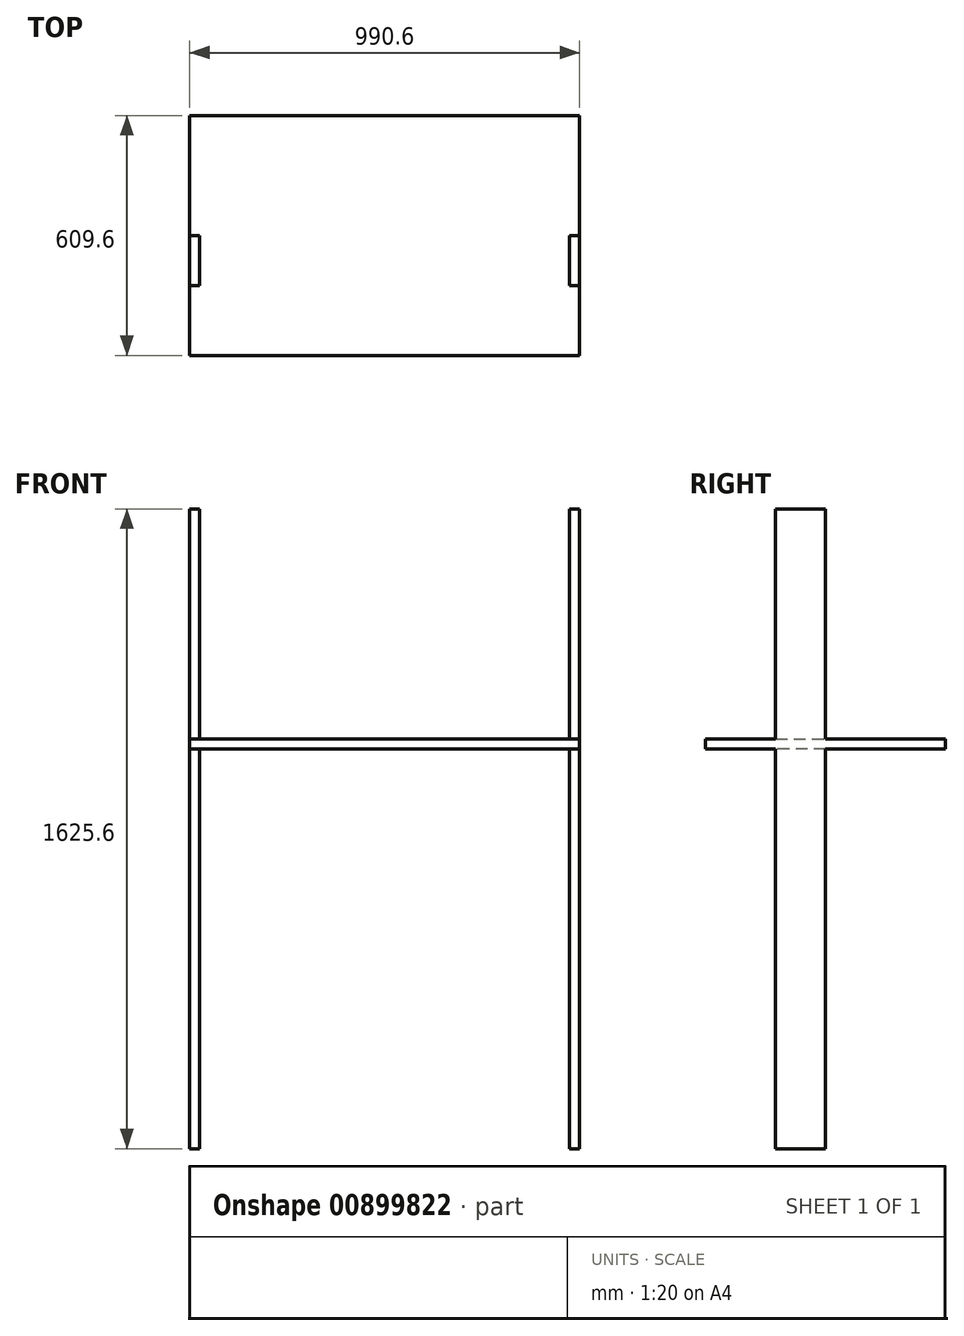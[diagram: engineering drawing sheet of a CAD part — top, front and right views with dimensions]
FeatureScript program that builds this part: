
annotation { "Feature Type Name" : "Feature", "Feature Type Description" : "" }
export const myFeature = defineFeature(function(context is Context, id is Id, definition is map)
    precondition{}
    {
        {
            var Q0;
            Q0=qCreatedBy(makeId("Top.planeOp"),FACE);
            var sketch = newSketch(context, id + "F0", { "sketchPlane" : qUnion([Q0])});
            skLineSegment(sketch, "E0.bottom", {"start": v(0, 0) * mm, "end": v(-990.6, 0) * mm});
            skLineSegment(sketch, "E0.top", {"start": v(0, 609.6) * mm, "end": v(-990.6, 609.6) * mm});
            skLineSegment(sketch, "E0.left", {"start": v(0, 0) * mm, "end": v(0, 609.6) * mm});
            skLineSegment(sketch, "E0.right", {"start": v(-990.6, 0) * mm, "end": v(-990.6, 609.6) * mm});
            skSolve(sketch);
        }
        {
            var Q0;
            Q0=makeQuery(id+"F0.imprint","IMPRINT",FACE,{"disambiguationData":[TD([[makeQuery(id+"F0.imprint","IMPRINT",EDGE,{"derivedFrom":sQuery(id+"F0.wireOp",EDGE,"E0.bottom")}),-1.0]])]});
            extrude(context, id + "F1", {"entities" : qUnion([Q0]), "depth" : 25.4 * mm, "offsetDistance" : 25.4 * mm});
        }
        {
            var Q0;
            Q0=makeQuery(id+"F1.opExtrude","CAP_FACE",FACE,{"disambiguationData":[OSD([sQuery(id+"F0.wireOp",EDGE,"E0.bottom"),sQuery(id+"F0.wireOp",EDGE,"E0.top"),sQuery(id+"F0.wireOp",EDGE,"E0.left"),sQuery(id+"F0.wireOp",EDGE,"E0.right")])],"isStart":true});
            var sketch = newSketch(context, id + "F2", { "sketchPlane" : qUnion([Q0])});
            skLineSegment(sketch, "E1.bottom", {"start": v(-990.6, -177.8) * mm, "end": v(-965.2, -177.8) * mm});
            skLineSegment(sketch, "E1.top", {"start": v(-990.6, -304.8) * mm, "end": v(-965.2, -304.8) * mm});
            skLineSegment(sketch, "E1.left", {"start": v(-990.6, -177.8) * mm, "end": v(-990.6, -304.8) * mm});
            skLineSegment(sketch, "E1.right", {"start": v(-965.2, -177.8) * mm, "end": v(-965.2, -304.8) * mm});
            skLineSegment(sketch, "E2.bottom", {"start": v(0, -304.8) * mm, "end": v(-25.4, -304.8) * mm});
            skLineSegment(sketch, "E2.top", {"start": v(0, -177.8) * mm, "end": v(-25.4, -177.8) * mm});
            skLineSegment(sketch, "E2.left", {"start": v(0, -304.8) * mm, "end": v(0, -177.8) * mm});
            skLineSegment(sketch, "E2.right", {"start": v(-25.4, -304.8) * mm, "end": v(-25.4, -177.8) * mm});
            skSolve(sketch);
        }
        {
            var Q0;
            Q0=makeQuery(id+"F2.imprint","IMPRINT",FACE,{"disambiguationData":[TD([[makeQuery(id+"F2.imprint","IMPRINT",EDGE,{"derivedFrom":sQuery(id+"F2.wireOp",EDGE,"E1.bottom")}),-1.0]])]});
            var Q1;
            Q1=makeQuery(id+"F2.imprint","IMPRINT",FACE,{"disambiguationData":[TD([[makeQuery(id+"F2.imprint","IMPRINT",EDGE,{"derivedFrom":sQuery(id+"F2.wireOp",EDGE,"E2.bottom")}),-1.0]])]});
            extrude(context, id + "F3", {"entities" : qUnion([Q0, Q1]), "operationType" : NewBodyOperationType.ADD, "depth" : 1016 * mm, "offsetDistance" : 25.4 * mm, "hasSecondDirection" : true, "secondDirectionOppositeDirection" : true, "secondDirectionDepth" : 609.6 * mm});
        }
    });
